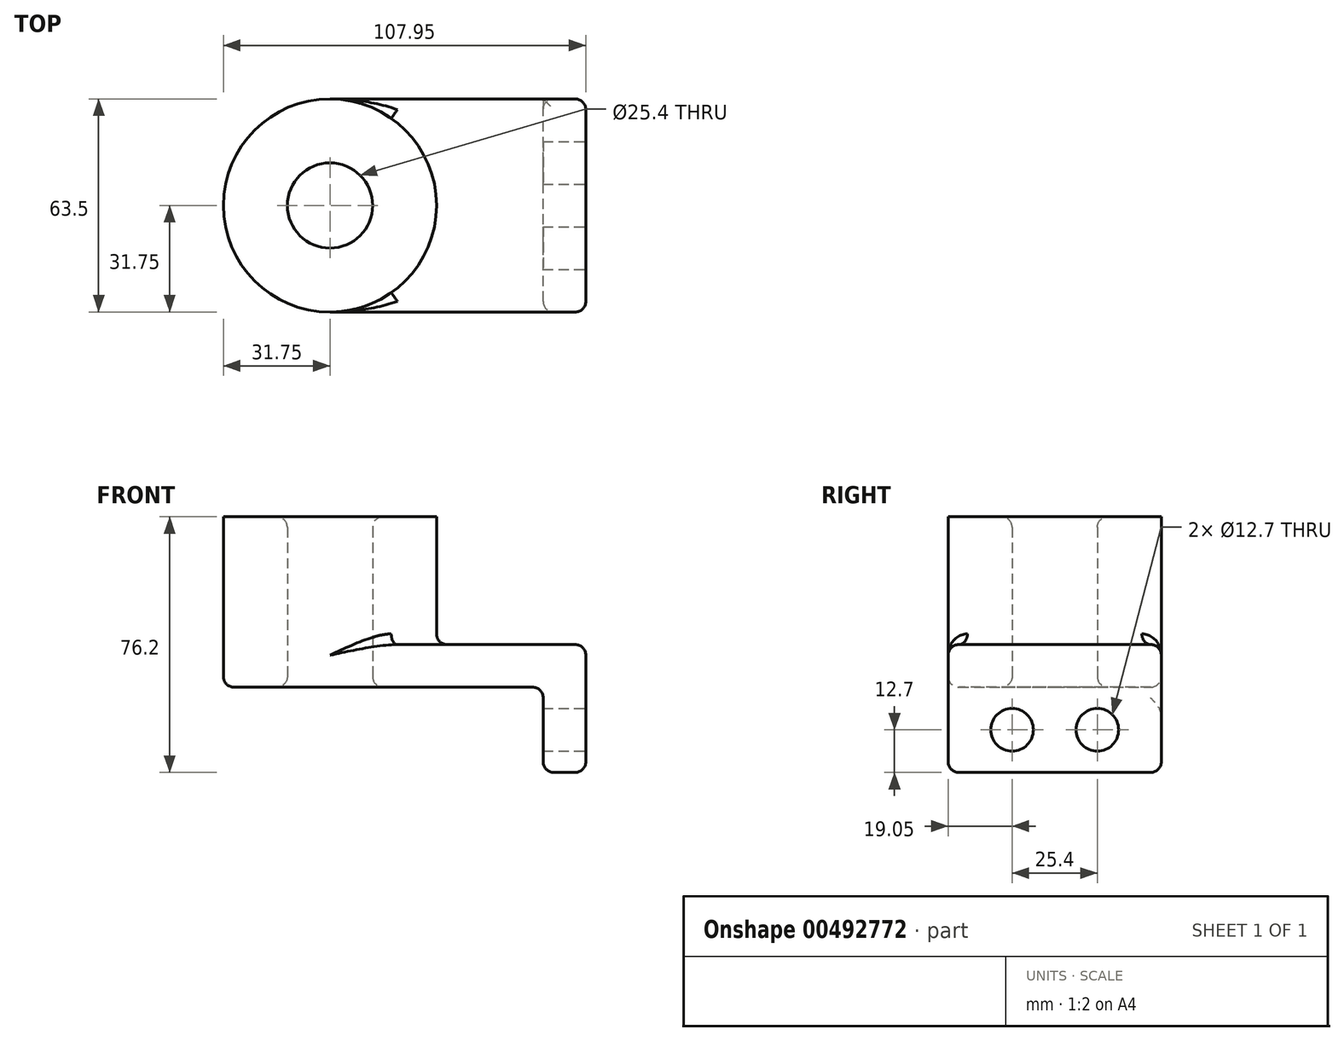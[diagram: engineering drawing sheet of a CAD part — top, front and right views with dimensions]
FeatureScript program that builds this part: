
annotation { "Feature Type Name" : "Feature", "Feature Type Description" : "" }
export const myFeature = defineFeature(function(context is Context, id is Id, definition is map)
    precondition{}
    {
        {
            var Q0;
            Q0=qCreatedBy(makeId("Top.planeOp"),FACE);
            var sketch = newSketch(context, id + "F0", { "sketchPlane" : qUnion([Q0])});
            skLineSegment(sketch, "E0.bottom", {"start": v(-38.1, -31.75) * mm, "end": v(38.1, -31.75) * mm});
            skLineSegment(sketch, "E0.top", {"start": v(-38.1, 31.75) * mm, "end": v(38.1, 31.75) * mm});
            skLineSegment(sketch, "E0.left", {"start": v(-38.1, -31.75) * mm, "end": v(-38.1, 31.75) * mm});
            skLineSegment(sketch, "E0.right", {"start": v(38.1, -31.75) * mm, "end": v(38.1, 31.75) * mm});
            skPoint(sketch, "E0.middle", {"position": v(0, 0) * mm});
            skCircle(sketch, "E1", {"center": v(-38.1, 0) * mm, "radius": 31.75 * mm});
            skCircle(sketch, "E2", {"center": v(-38.1, 0) * mm, "radius": 12.7 * mm});
            skSolve(sketch);
        }
        {
            var Q0;
            Q0 = qSketchRegion(id + "F0", true);
            extrude(context, id + "F1", {"entities" : qUnion([Q0]), "depth" : 12.7 * mm});
        }
        {
            var Q0;
            {var subQ1=sQuery(id+"F0.wireOp",EDGE,"E0.left");var subQ3=sQuery(id+"F0.wireOp",EDGE,"E2");var subQ4=makeQuery(id+"F0.imprint","INTERSECT",VERTEX,{"disambiguationData":[OD(0.0)],"derivedFrom":[subQ1,subQ3]});Q0=makeQuery(id+"F0.imprint","IMPRINT",FACE,{"disambiguationData":[TD([[makeQuery(id+"F0.imprint","IMPRINT",EDGE,{"disambiguationData":[TD([[subQ4,1.0]])],"derivedFrom":subQ3}),-1.0]])]});}
            var Q1;
            {var subQ1=sQuery(id+"F0.wireOp",EDGE,"E0.left");var subQ3=sQuery(id+"F0.wireOp",EDGE,"E2");var subQ4=makeQuery(id+"F0.imprint","INTERSECT",VERTEX,{"disambiguationData":[OD(0.0)],"derivedFrom":[subQ1,subQ3]});Q1=makeQuery(id+"F0.imprint","IMPRINT",FACE,{"disambiguationData":[TD([[makeQuery(id+"F0.imprint","IMPRINT",EDGE,{"disambiguationData":[TD([[subQ4,-1.0]])],"derivedFrom":subQ3}),-1.0]])]});}
            extrude(context, id + "F2", {"entities" : qUnion([Q0, Q1]), "operationType" : NewBodyOperationType.ADD, "depth" : 50.8 * mm});
        }
        {
            var Q0;
            Q0=makeQuery(id+"F1.opExtrude","SWEPT_FACE",FACE,{"disambiguationData":[OSD([sQuery(id+"F0.wireOp",EDGE,"E0.right")])]});
            var sketch = newSketch(context, id + "F3", { "sketchPlane" : qUnion([Q0])});
            skLineSegment(sketch, "E3.bottom", {"start": v(-31.75, 12.7) * mm, "end": v(31.75, 12.7) * mm});
            skLineSegment(sketch, "E3.top", {"start": v(-31.75, -25.4) * mm, "end": v(31.75, -25.4) * mm});
            skLineSegment(sketch, "E3.left", {"start": v(-31.75, 12.7) * mm, "end": v(-31.75, -25.4) * mm});
            skLineSegment(sketch, "E3.right", {"start": v(31.75, 12.7) * mm, "end": v(31.75, -25.4) * mm});
            skCircle(sketch, "E4", {"center": v(-12.7, -12.7) * mm, "radius": 6.35 * mm});
            skLineSegment(sketch, "E5", {"start": v(0, 0) * mm, "end": v(0, -25.4) * mm});
            skCircle(sketch, "E6.MirrorC", {"center": v(12.7, -12.7) * mm, "radius": 6.35 * mm});
            skSolve(sketch);
        }
        {
            var Q0;
            {var subQ0=sQuery(id+"F3.wireOp",EDGE,"E5");Q0=makeQuery(id+"F3.imprint","IMPRINT",FACE,{"disambiguationData":[TD([[makeQuery(id+"F3.imprint","IMPRINT",EDGE,{"derivedFrom":subQ0}),1.0]])]});}
            var Q1;
            Q1=makeQuery(id+"F3.imprint","IMPRINT",FACE,{"disambiguationData":[TD([[makeQuery(id+"F3.imprint","IMPRINT",EDGE,{"derivedFrom":sQuery(id+"F3.wireOp",EDGE,"E4")}),-1.0]])]});
            var Q2;
            {var subQ3=sQuery(id+"F3.wireOp",EDGE,"E3.bottom");Q2=makeQuery(id+"F3.imprint","IMPRINT",FACE,{"disambiguationData":[TD([[makeQuery(id+"F3.imprint","IMPRINT",EDGE,{"derivedFrom":subQ3}),-1.0]])]});}
            extrude(context, id + "F4", {"entities" : qUnion([Q0, Q1, Q2]), "operationType" : NewBodyOperationType.ADD, "oppositeDirection" : true, "depth" : 12.7 * mm});
        }
        {
            var Q0;
            {var subQ0=sQuery(id+"F0.wireOp",EDGE,"E1");Q0=makeQuery(id+"F2.boolean.opBoolean","INTERSECT",EDGE,{"derivedFrom":[makeQuery(id+"F1.opExtrude","CAP_FACE",FACE,{"disambiguationData":[OSD([sQuery(id+"F0.wireOp",EDGE,"E0.bottom"),sQuery(id+"F0.wireOp",EDGE,"E0.top"),sQuery(id+"F0.wireOp",EDGE,"E0.right"),subQ0,sQuery(id+"F0.wireOp",EDGE,"E2")])],"isStart":false}),makeQuery(id+"F2.opExtrude","SWEPT_FACE",FACE,{"disambiguationData":[OSD([subQ0])]})]});}
            var Q1;
            Q1=makeQuery(id+"F4.opExtrude","CAP_EDGE",EDGE,{"disambiguationData":[OSD([sQuery(id+"F3.wireOp",EDGE,"E3.top")])],"isStart":true});
            var Q2;
            Q2=makeQuery(id+"F1.opExtrude","CAP_EDGE",EDGE,{"disambiguationData":[OSD([sQuery(id+"F0.wireOp",EDGE,"E0.right")])],"isStart":false});
            var Q3;
            Q3=makeQuery(id+"F4.opExtrude","CAP_EDGE",EDGE,{"disambiguationData":[OSD([sQuery(id+"F3.wireOp",EDGE,"E3.top")])],"isStart":false});
            var Q4;
            Q4=makeQuery(id+"F4.boolean.opBoolean","INTERSECT",EDGE,{"derivedFrom":[makeQuery(id+"F1.opExtrude","CAP_FACE",FACE,{"disambiguationData":[OSD([sQuery(id+"F0.wireOp",EDGE,"E0.bottom"),sQuery(id+"F0.wireOp",EDGE,"E0.top"),sQuery(id+"F0.wireOp",EDGE,"E0.right"),sQuery(id+"F0.wireOp",EDGE,"E1"),sQuery(id+"F0.wireOp",EDGE,"E2")])],"isStart":true}),makeQuery(id+"F4.opExtrude","CAP_FACE",FACE,{"disambiguationData":[OSD([sQuery(id+"F3.wireOp",EDGE,"E3.bottom"),sQuery(id+"F3.wireOp",EDGE,"E3.top"),sQuery(id+"F3.wireOp",EDGE,"E3.left"),sQuery(id+"F3.wireOp",EDGE,"E3.right"),sQuery(id+"F3.wireOp",EDGE,"E4"),sQuery(id+"F3.wireOp",EDGE,"E6.MirrorC")])],"isStart":false})]});
            var Q5;
            Q5=makeQuery(id+"F1.opExtrude","CAP_EDGE",EDGE,{"disambiguationData":[OSD([sQuery(id+"F0.wireOp",EDGE,"E0.bottom")])],"isStart":false});
            var Q6;
            Q6=makeQuery(id+"F1.opExtrude","CAP_EDGE",EDGE,{"disambiguationData":[OSD([sQuery(id+"F0.wireOp",EDGE,"E0.top")])],"isStart":false});
            var Q7;
            Q7=makeQuery(id+"F2.opExtrude","CAP_EDGE",EDGE,{"disambiguationData":[OSD([sQuery(id+"F0.wireOp",EDGE,"E2")])],"isStart":false});
            var Q8;
            Q8=makeQuery(id+"F1.opExtrude","CAP_EDGE",EDGE,{"disambiguationData":[OSD([sQuery(id+"F0.wireOp",EDGE,"E0.bottom")])],"isStart":true});
            var Q9;
            Q9=makeQuery(id+"F1.opExtrude","CAP_EDGE",EDGE,{"disambiguationData":[OSD([sQuery(id+"F0.wireOp",EDGE,"E0.top")])],"isStart":true});
            var Q10;
            Q10=makeQuery(id+"F4.boolean.opBoolean","MERGE",EDGE,{"derivedFrom":[makeQuery(id+"F1.opExtrude","SWEPT_EDGE",EDGE,{"disambiguationData":[OSD([sQuery(id+"F0.wireOp",EDGE,"E0.bottom"),sQuery(id+"F0.wireOp",EDGE,"E0.right")])]}),makeQuery(id+"F4.opExtrude","CAP_EDGE",EDGE,{"disambiguationData":[OSD([sQuery(id+"F3.wireOp",EDGE,"E3.left")])],"isStart":true})]});
            var Q11;
            Q11=makeQuery(id+"F4.opExtrude","CAP_EDGE",EDGE,{"disambiguationData":[OSD([sQuery(id+"F3.wireOp",EDGE,"E3.left")])],"isStart":false});
            var Q12;
            Q12=makeQuery(id+"F4.boolean.opBoolean","MERGE",EDGE,{"derivedFrom":[makeQuery(id+"F1.opExtrude","SWEPT_EDGE",EDGE,{"disambiguationData":[OSD([sQuery(id+"F0.wireOp",EDGE,"E0.top"),sQuery(id+"F0.wireOp",EDGE,"E0.right")])]}),makeQuery(id+"F4.opExtrude","CAP_EDGE",EDGE,{"disambiguationData":[OSD([sQuery(id+"F3.wireOp",EDGE,"E3.right")])],"isStart":true})]});
            var Q13;
            Q13=makeQuery(id+"F4.opExtrude","SWEPT_EDGE",EDGE,{"disambiguationData":[OSD([sQuery(id+"F3.wireOp",EDGE,"E3.top"),sQuery(id+"F3.wireOp",EDGE,"E3.right")])]});
            var Q14;
            Q14=makeQuery(id+"F4.opExtrude","SWEPT_EDGE",EDGE,{"disambiguationData":[OSD([sQuery(id+"F3.wireOp",EDGE,"E3.top"),sQuery(id+"F3.wireOp",EDGE,"E3.left")])]});
            var Q15;
            Q15=makeQuery(id+"F1.opExtrude","CAP_EDGE",EDGE,{"disambiguationData":[OSD([sQuery(id+"F0.wireOp",EDGE,"E2")])],"isStart":true});
            fillet(context, id + "F5", {"entities" : qUnion([Q0, Q1, Q2, Q3, Q4, Q5, Q6, Q7, Q8, Q9, Q10, Q11, Q12, Q13, Q14, Q15]), "radius" : 3.17 * mm, "tangentPropagation" : true, "allowEdgeOverflow" : false});
        }
    });
